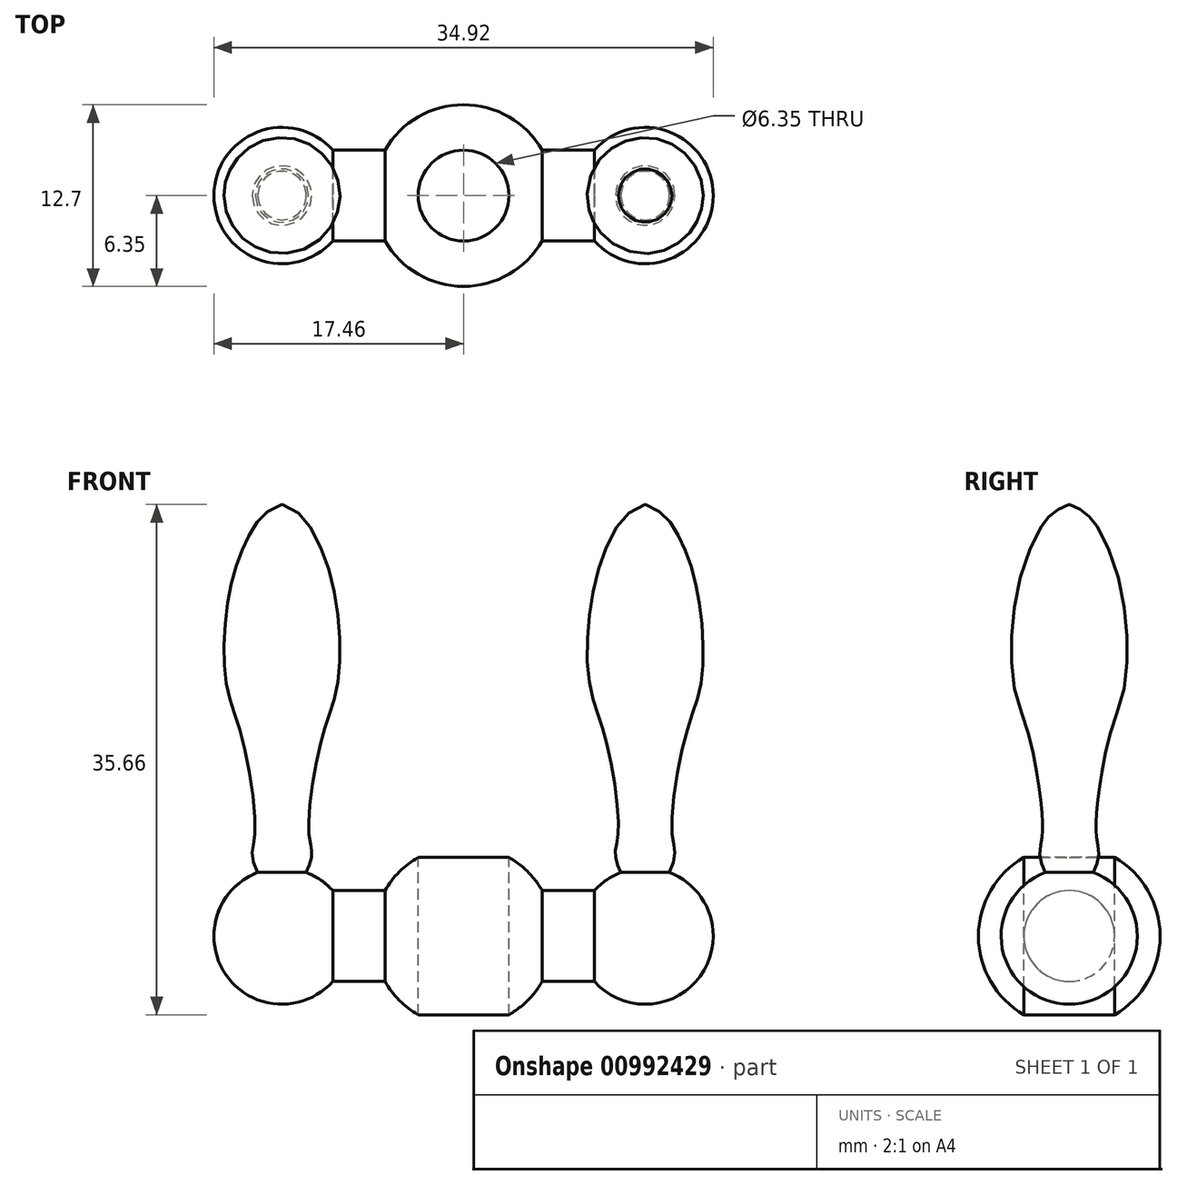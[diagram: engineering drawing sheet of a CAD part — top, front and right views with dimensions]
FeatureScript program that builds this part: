
annotation { "Feature Type Name" : "Feature", "Feature Type Description" : "" }
export const myFeature = defineFeature(function(context is Context, id is Id, definition is map)
    precondition{}
    {
        {
            var Q0;
            Q0=qCreatedBy(makeId("Front.planeOp"),FACE);
            var sketch = newSketch(context, id + "F0", { "sketchPlane" : qUnion([Q0])});
            skCircle(sketch, "E0", {"center": v(0, 0) * mm, "radius": 6.35 * mm});
            skLineSegment(sketch, "E1", {"start": v(0, 50.8) * mm, "end": v(0, -50.8) * mm});
            skLineSegment(sketch, "E2", {"start": v(-50.8, 0) * mm, "end": v(50.8, 0) * mm});
            skCircle(sketch, "E3", {"center": v(-12.7, 0) * mm, "radius": 4.76 * mm});
            skCircle(sketch, "E4", {"center": v(12.7, 0) * mm, "radius": 4.76 * mm});
            skLineSegment(sketch, "E5.bottom", {"start": v(-12.7, -3.17) * mm, "end": v(12.7, -3.17) * mm});
            skLineSegment(sketch, "E5.top", {"start": v(-12.7, 3.18) * mm, "end": v(12.7, 3.18) * mm});
            skLineSegment(sketch, "E5.left", {"start": v(-12.7, -3.17) * mm, "end": v(-12.7, 3.18) * mm});
            skLineSegment(sketch, "E5.right", {"start": v(12.7, -3.17) * mm, "end": v(12.7, 3.18) * mm});
            skLineSegment(sketch, "E6", {"start": v(-12.7, 4.76) * mm, "end": v(-12.7, 30.16) * mm});
            skFitSpline(sketch, "E7", {"points": [v(-12.7, 30.16) * mm, v(-15.09, 27.85) * mm, v(-16.45, 23.55) * mm, v(-16.6, 17.67) * mm, v(-15.51, 13.92) * mm, v(-14.57, 7.26) * mm, v(-14.78, 5.86) * mm, v(-14.4, 4.45) * mm], "startDerivative": vector(-26.43, -7.48) * mm, "endDerivative": vector(8.71, -16.43) * mm});
            skFitSpline(sketch, "E8.MirrorCS", {"points": [v(12.7, 30.16) * mm, v(15.09, 27.85) * mm, v(16.45, 23.55) * mm, v(16.6, 17.67) * mm, v(15.51, 13.92) * mm, v(14.57, 7.26) * mm, v(14.78, 5.86) * mm, v(14.4, 4.45) * mm], "startDerivative": vector(26.43, -7.48) * mm, "endDerivative": vector(-8.71, -16.43) * mm});
            skLineSegment(sketch, "E9.MirrorCS", {"start": v(12.7, 4.76) * mm, "end": v(12.7, 30.16) * mm});
            skLineSegment(sketch, "E10.bottom", {"start": v(3.18, 12.7) * mm, "end": v(-3.17, 12.7) * mm});
            skLineSegment(sketch, "E10.top", {"start": v(3.17, -12.7) * mm, "end": v(-3.18, -12.7) * mm});
            skLineSegment(sketch, "E10.left", {"start": v(3.18, 12.7) * mm, "end": v(3.17, -12.7) * mm});
            skLineSegment(sketch, "E10.right", {"start": v(-3.17, 12.7) * mm, "end": v(-3.18, -12.7) * mm});
            skSolve(sketch);
        }
        {
            var Q0;
            {var subQ0=sQuery(id+"F0.wireOp",EDGE,"E10.right");var subQ1=sQuery(id+"F0.wireOp",EDGE,"E0");var subQ2=makeQuery(id+"F0.imprint","INTERSECT",VERTEX,{"disambiguationData":[OD(0.0)],"derivedFrom":[subQ1,subQ0]});Q0=makeQuery(id+"F0.imprint","IMPRINT",FACE,{"disambiguationData":[TD([[makeQuery(id+"F0.imprint","IMPRINT",EDGE,{"disambiguationData":[TD([[subQ2,-1.0]])],"derivedFrom":subQ1}),1.0]])]});}
            var Q1;
            {var subQ0=sQuery(id+"F0.wireOp",EDGE,"E5.top");var subQ1=sQuery(id+"F0.wireOp",EDGE,"E0");var subQ2=makeQuery(id+"F0.imprint","INTERSECT",VERTEX,{"disambiguationData":[OD(1.0)],"derivedFrom":[subQ1,subQ0]});Q1=makeQuery(id+"F0.imprint","IMPRINT",FACE,{"disambiguationData":[TD([[makeQuery(id+"F0.imprint","IMPRINT",EDGE,{"disambiguationData":[TD([[subQ2,-1.0]])],"derivedFrom":subQ1}),1.0]])]});}
            var Q2;
            {var subQ0=sQuery(id+"F0.wireOp",EDGE,"E5.bottom");var subQ1=sQuery(id+"F0.wireOp",EDGE,"E0");var subQ2=makeQuery(id+"F0.imprint","INTERSECT",VERTEX,{"disambiguationData":[OD(0.0)],"derivedFrom":[subQ1,subQ0]});Q2=makeQuery(id+"F0.imprint","IMPRINT",FACE,{"disambiguationData":[TD([[makeQuery(id+"F0.imprint","IMPRINT",EDGE,{"disambiguationData":[TD([[subQ2,1.0]])],"derivedFrom":subQ1}),1.0]])]});}
            var Q3;
            {var subQ0=sQuery(id+"F0.wireOp",EDGE,"E5.bottom");var subQ1=sQuery(id+"F0.wireOp",EDGE,"E0");var subQ2=makeQuery(id+"F0.imprint","INTERSECT",VERTEX,{"disambiguationData":[OD(0.0)],"derivedFrom":[subQ1,subQ0]});Q3=makeQuery(id+"F0.imprint","IMPRINT",FACE,{"disambiguationData":[TD([[makeQuery(id+"F0.imprint","IMPRINT",EDGE,{"disambiguationData":[TD([[subQ2,-1.0]])],"derivedFrom":subQ1}),1.0]])]});}
            var Q4;
            Q4=sQuery(id+"F0.wireOp",EDGE,"E1");
            revolve(context, id + "F1", {"surfaceOperationType" : NewSurfaceOperationType.NEW, "entities" : qUnion([Q0, Q1, Q2, Q3]), "axis" : qUnion([Q4]), "revolveType" : RevolveType.FULL});
        }
        {
            var Q0;
            {var subQ0=sQuery(id+"F0.wireOp",EDGE,"E3");var subQ2=sQuery(id+"F0.wireOp",EDGE,"E2");var subQ3=makeQuery(id+"F0.imprint","INTERSECT",VERTEX,{"disambiguationData":[OD(0.0)],"derivedFrom":[subQ2,subQ0]});Q0=makeQuery(id+"F0.imprint","IMPRINT",FACE,{"disambiguationData":[TD([[makeQuery(id+"F0.imprint","IMPRINT",EDGE,{"disambiguationData":[TD([[subQ3,-1.0]])],"derivedFrom":subQ2}),1.0]])]});}
            var Q1;
            {var subQ0=sQuery(id+"F0.wireOp",EDGE,"E5.left");var subQ1=sQuery(id+"F0.wireOp",EDGE,"E2");var subQ2=makeQuery(id+"F0.imprint","INTERSECT",VERTEX,{"derivedFrom":[subQ1,subQ0]});Q1=makeQuery(id+"F0.imprint","IMPRINT",FACE,{"disambiguationData":[TD([[makeQuery(id+"F0.imprint","IMPRINT",EDGE,{"disambiguationData":[TD([[subQ2,-1.0]])],"derivedFrom":subQ1}),1.0]])]});}
            var Q2;
            {var subQ0=sQuery(id+"F0.wireOp",EDGE,"E4");var subQ1=sQuery(id+"F0.wireOp",EDGE,"E2");var subQ2=makeQuery(id+"F0.imprint","INTERSECT",VERTEX,{"disambiguationData":[OD(1.0)],"derivedFrom":[subQ1,subQ0]});Q2=makeQuery(id+"F0.imprint","IMPRINT",FACE,{"disambiguationData":[TD([[makeQuery(id+"F0.imprint","IMPRINT",EDGE,{"disambiguationData":[TD([[subQ2,-1.0]])],"derivedFrom":subQ1}),1.0]])]});}
            var Q3;
            {var subQ0=sQuery(id+"F0.wireOp",EDGE,"E4");var subQ5=sQuery(id+"F0.wireOp",EDGE,"E2");var subQ6=makeQuery(id+"F0.imprint","INTERSECT",VERTEX,{"disambiguationData":[OD(0.0)],"derivedFrom":[subQ5,subQ0]});Q3=makeQuery(id+"F0.imprint","IMPRINT",FACE,{"disambiguationData":[TD([[makeQuery(id+"F0.imprint","IMPRINT",EDGE,{"disambiguationData":[TD([[subQ6,1.0]])],"derivedFrom":subQ5}),1.0]])]});}
            var Q4;
            {var subQ0=sQuery(id+"F0.wireOp",EDGE,"E5.top");var subQ1=sQuery(id+"F0.wireOp",EDGE,"E0");var subQ2=makeQuery(id+"F0.imprint","INTERSECT",VERTEX,{"disambiguationData":[OD(0.0)],"derivedFrom":[subQ1,subQ0]});Q4=makeQuery(id+"F0.imprint","IMPRINT",FACE,{"disambiguationData":[TD([[makeQuery(id+"F0.imprint","IMPRINT",EDGE,{"disambiguationData":[TD([[subQ2,1.0]])],"derivedFrom":subQ1}),-1.0]])]});}
            var Q5;
            {var subQ0=sQuery(id+"F0.wireOp",EDGE,"E5.top");var subQ1=sQuery(id+"F0.wireOp",EDGE,"E0");var subQ2=makeQuery(id+"F0.imprint","INTERSECT",VERTEX,{"disambiguationData":[OD(1.0)],"derivedFrom":[subQ1,subQ0]});Q5=makeQuery(id+"F0.imprint","IMPRINT",FACE,{"disambiguationData":[TD([[makeQuery(id+"F0.imprint","IMPRINT",EDGE,{"disambiguationData":[TD([[subQ2,-1.0]])],"derivedFrom":subQ1}),-1.0]])]});}
            var Q6;
            Q6=sQuery(id+"F0.wireOp",EDGE,"E2");
            revolve(context, id + "F2", {"operationType" : NewBodyOperationType.ADD, "surfaceOperationType" : NewSurfaceOperationType.NEW, "entities" : qUnion([Q0, Q1, Q2, Q3, Q4, Q5]), "axis" : qUnion([Q6]), "revolveType" : RevolveType.FULL});
        }
        {
            var Q0;
            {var subQ0=sQuery(id+"F0.wireOp",EDGE,"E6");Q0=makeQuery(id+"F0.imprint","IMPRINT",FACE,{"disambiguationData":[TD([[makeQuery(id+"F0.imprint","IMPRINT",EDGE,{"derivedFrom":subQ0}),1.0]])]});}
            var Q1;
            Q1=sQuery(id+"F0.wireOp",EDGE,"E6");
            revolve(context, id + "F3", {"operationType" : NewBodyOperationType.ADD, "surfaceOperationType" : NewSurfaceOperationType.NEW, "entities" : qUnion([Q0]), "axis" : qUnion([Q1]), "revolveType" : RevolveType.FULL});
        }
        {
            var Q0;
            {var subQ0=sQuery(id+"F0.wireOp",EDGE,"E8.MirrorCS");Q0=makeQuery(id+"F0.imprint","IMPRINT",FACE,{"disambiguationData":[TD([[makeQuery(id+"F0.imprint","IMPRINT",EDGE,{"derivedFrom":subQ0}),-1.0]])]});}
            var Q1;
            Q1=sQuery(id+"F0.wireOp",EDGE,"E9.MirrorCS");
            revolve(context, id + "F4", {"operationType" : NewBodyOperationType.ADD, "surfaceOperationType" : NewSurfaceOperationType.NEW, "entities" : qUnion([Q0]), "axis" : qUnion([Q1]), "revolveType" : RevolveType.FULL});
        }
    });
